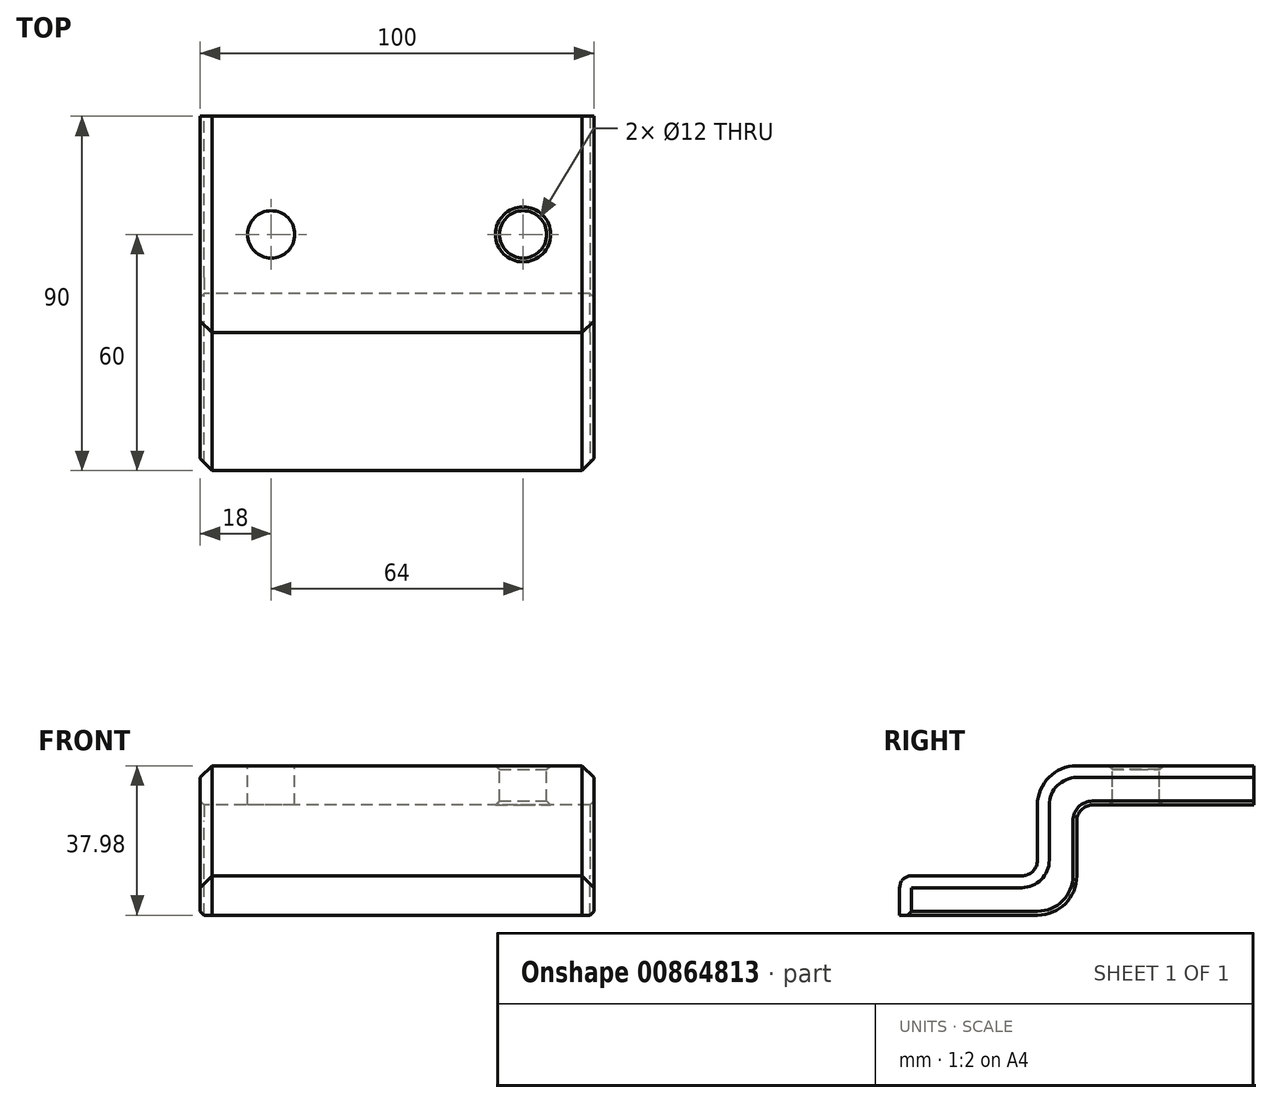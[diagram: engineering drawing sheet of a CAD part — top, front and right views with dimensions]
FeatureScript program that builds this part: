
annotation { "Feature Type Name" : "Feature", "Feature Type Description" : "" }
export const myFeature = defineFeature(function(context is Context, id is Id, definition is map)
    precondition{}
    {
        {
            var Q0;
            Q0=qCreatedBy(makeId("Right.planeOp"),FACE);
            var sketch = newSketch(context, id + "F0", { "sketchPlane" : qUnion([Q0])});
            skLineSegment(sketch, "E0", {"start": v(0, 75.8) * mm, "end": v(0, -75.8) * mm, "construction": true});
            skLineSegment(sketch, "E1", {"start": v(0, 36.2) * mm, "end": v(-45, 36.2) * mm});
            skLineSegment(sketch, "E2", {"start": v(-55, 26.2) * mm, "end": v(-55, 12.2) * mm});
            skLineSegment(sketch, "E3", {"start": v(-59, 8.2) * mm, "end": v(-87, 8.2) * mm});
            skLineSegment(sketch, "E4", {"start": v(-90, 5.2) * mm, "end": v(-90, -1.8) * mm});
            skLineSegment(sketch, "E5", {"start": v(0, 26.2) * mm, "end": v(0, 36.2) * mm});
            skPoint(sketch, "E6.visualSharp", {"position": v(-55, 36.2) * mm});
            skArc(sketch, "E6.filletArc", {"start": v(-45, 36.2) * mm, "mid": v(-52.07, 33.26) * mm, "end": v(-55, 26.2) * mm});
            skArc(sketch, "E7.filletArc", {"start": v(-59, 8.2) * mm, "mid": v(-56.17, 9.38) * mm, "end": v(-55, 12.2) * mm});
            skPoint(sketch, "E8.visualSharp", {"position": v(-90, 8.2) * mm});
            skArc(sketch, "E8.filletArc", {"start": v(-87, 8.2) * mm, "mid": v(-89.12, 7.33) * mm, "end": v(-90, 5.2) * mm});
            skLineSegment(sketch, "E9", {"start": v(0, 26.2) * mm, "end": v(-41, 26.2) * mm});
            skLineSegment(sketch, "E10", {"start": v(-90, -1.8) * mm, "end": v(-55, -1.8) * mm});
            skLineSegment(sketch, "E11", {"start": v(-45, 8.2) * mm, "end": v(-45, 22.2) * mm});
            skPoint(sketch, "E12.visualSharp", {"position": v(-45, -1.8) * mm});
            skArc(sketch, "E12.filletArc", {"start": v(-55, -1.8) * mm, "mid": v(-47.93, 1.14) * mm, "end": v(-45, 8.2) * mm});
            skArc(sketch, "E13.filletArc", {"start": v(-41, 26.2) * mm, "mid": v(-43.83, 25.02) * mm, "end": v(-45, 22.2) * mm});
            skArc(sketch, "E14.MirrorCS", {"start": v(59, 8.2) * mm, "mid": v(56.17, 9.38) * mm, "end": v(55, 12.2) * mm});
            skArc(sketch, "E15.MirrorCS", {"start": v(87, 8.2) * mm, "mid": v(89.12, 7.33) * mm, "end": v(90, 5.2) * mm});
            skArc(sketch, "E16.MirrorCS", {"start": v(41, 26.2) * mm, "mid": v(43.83, 25.02) * mm, "end": v(45, 22.2) * mm});
            skLineSegment(sketch, "E17.MirrorCS", {"start": v(90, -1.8) * mm, "end": v(55, -1.8) * mm});
            skLineSegment(sketch, "E18.MirrorCS", {"start": v(55, 26.2) * mm, "end": v(55, 12.2) * mm});
            skPoint(sketch, "E19.MirrorP", {"position": v(45, -1.8) * mm});
            skPoint(sketch, "E20.MirrorP", {"position": v(90, 8.2) * mm});
            skLineSegment(sketch, "E21.MirrorCS", {"start": v(90, 5.2) * mm, "end": v(90, -1.8) * mm});
            skPoint(sketch, "E22.MirrorP", {"position": v(55, 36.2) * mm});
            skPoint(sketch, "E23.MirrorP", {"position": v(45, 26.2) * mm});
            skLineSegment(sketch, "E24.MirrorCS", {"start": v(45, 8.2) * mm, "end": v(45, 22.2) * mm});
            skLineSegment(sketch, "E25.MirrorCS", {"start": v(0, 26.2) * mm, "end": v(41, 26.2) * mm});
            skArc(sketch, "E26.MirrorCS", {"start": v(45, 36.2) * mm, "mid": v(52.07, 33.26) * mm, "end": v(55, 26.2) * mm});
            skLineSegment(sketch, "E27.MirrorCS", {"start": v(59, 8.2) * mm, "end": v(87, 8.2) * mm});
            skArc(sketch, "E28.MirrorCS", {"start": v(55, -1.8) * mm, "mid": v(47.93, 1.14) * mm, "end": v(45, 8.2) * mm});
            skLineSegment(sketch, "E29.MirrorCS", {"start": v(0, 36.2) * mm, "end": v(45, 36.2) * mm});
            skSolve(sketch);
        }
        {
            var Q0;
            Q0=makeQuery(id+"F0.imprint","IMPRINT",FACE,{"disambiguationData":[TD([[makeQuery(id+"F0.imprint","IMPRINT",EDGE,{"derivedFrom":sQuery(id+"F0.wireOp",EDGE,"E14.MirrorCS")}),1.0]])]});
            var Q1;
            Q1=makeQuery(id+"F0.imprint","IMPRINT",FACE,{"disambiguationData":[TD([[makeQuery(id+"F0.imprint","IMPRINT",EDGE,{"derivedFrom":sQuery(id+"F0.wireOp",EDGE,"E1")}),1.0]])]});
            extrude(context, id + "F1", {"entities" : qUnion([Q0, Q1]), "depth" : 100 * mm, "offsetDistance" : 25 * mm});
        }
        {
            var Q0;
            Q0=makeQuery(id+"F1.opExtrude","CAP_EDGE",EDGE,{"disambiguationData":[OSD([sQuery(id+"F0.wireOp",EDGE,"E4")])],"isStart":true});
            var Q1;
            Q1=makeQuery(id+"F1.opExtrude","CAP_EDGE",EDGE,{"disambiguationData":[OSD([sQuery(id+"F0.wireOp",EDGE,"E8.filletArc")])],"isStart":true});
            var Q2;
            Q2=makeQuery(id+"F1.opExtrude","CAP_EDGE",EDGE,{"disambiguationData":[OSD([sQuery(id+"F0.wireOp",EDGE,"E3")])],"isStart":true});
            var Q3;
            Q3=makeQuery(id+"F1.opExtrude","CAP_EDGE",EDGE,{"disambiguationData":[OSD([sQuery(id+"F0.wireOp",EDGE,"E7.filletArc")])],"isStart":true});
            var Q4;
            Q4=makeQuery(id+"F1.opExtrude","CAP_EDGE",EDGE,{"disambiguationData":[OSD([sQuery(id+"F0.wireOp",EDGE,"E2")])],"isStart":true});
            var Q5;
            Q5=makeQuery(id+"F1.opExtrude","CAP_EDGE",EDGE,{"disambiguationData":[OSD([sQuery(id+"F0.wireOp",EDGE,"E6.filletArc")])],"isStart":true});
            var Q6;
            Q6=makeQuery(id+"F1.opExtrude","CAP_EDGE",EDGE,{"disambiguationData":[OSD([sQuery(id+"F0.wireOp",EDGE,"E1"),sQuery(id+"F0.wireOp",EDGE,"E29.MirrorCS")])],"isStart":true});
            var Q7;
            Q7=makeQuery(id+"F1.opExtrude","CAP_EDGE",EDGE,{"disambiguationData":[OSD([sQuery(id+"F0.wireOp",EDGE,"E26.MirrorCS")])],"isStart":true});
            var Q8;
            Q8=makeQuery(id+"F1.opExtrude","CAP_EDGE",EDGE,{"disambiguationData":[OSD([sQuery(id+"F0.wireOp",EDGE,"E1"),sQuery(id+"F0.wireOp",EDGE,"E29.MirrorCS")])],"isStart":false});
            chamfer(context, id + "F2", {"entities" : qUnion([Q0, Q1, Q2, Q3, Q4, Q5, Q6, Q7, Q8]), "width" : 3 * mm, "tangentPropagation" : true});
        }
        {
            var Q0;
            Q0=makeQuery(id+"F1.opExtrude","CAP_EDGE",EDGE,{"disambiguationData":[OSD([sQuery(id+"F0.wireOp",EDGE,"E9"),sQuery(id+"F0.wireOp",EDGE,"E25.MirrorCS")])],"isStart":false});
            var Q1;
            Q1=makeQuery(id+"F1.opExtrude","CAP_EDGE",EDGE,{"disambiguationData":[OSD([sQuery(id+"F0.wireOp",EDGE,"E9"),sQuery(id+"F0.wireOp",EDGE,"E25.MirrorCS")])],"isStart":true});
            chamfer(context, id + "F3", {"entities" : qUnion([Q0, Q1]), "width" : 1 * mm, "tangentPropagation" : true});
        }
        {
            var Q0;
            Q0=makeQuery(id+"F1.opExtrude","SWEPT_FACE",FACE,{"disambiguationData":[OSD([sQuery(id+"F0.wireOp",EDGE,"E1"),sQuery(id+"F0.wireOp",EDGE,"E29.MirrorCS")])]});
            var sketch = newSketch(context, id + "F4", { "sketchPlane" : qUnion([Q0])});
            skLineSegment(sketch, "E30", {"start": v(3, 30) * mm, "end": v(97, 30) * mm, "construction": true});
            skLineSegment(sketch, "E31", {"start": v(3, -30) * mm, "end": v(97, -30) * mm, "construction": true});
            skLineSegment(sketch, "E32", {"start": v(18, 45) * mm, "end": v(18, -45) * mm, "construction": true});
            skLineSegment(sketch, "E33", {"start": v(82, 45) * mm, "end": v(82, -45) * mm, "construction": true});
            skCircle(sketch, "E34", {"center": v(18, 30) * mm, "radius": 6 * mm});
            skCircle(sketch, "E35", {"center": v(82, 30) * mm, "radius": 6 * mm});
            skCircle(sketch, "E36", {"center": v(82, -30) * mm, "radius": 6 * mm});
            skCircle(sketch, "E37", {"center": v(18, -30) * mm, "radius": 6 * mm});
            skSolve(sketch);
        }
        {
            var Q0;
            Q0=makeQuery(id+"F4.imprint","IMPRINT",FACE,{"disambiguationData":[TD([[makeQuery(id+"F4.imprint","IMPRINT",EDGE,{"derivedFrom":sQuery(id+"F4.wireOp",EDGE,"E37")}),1.0]])]});
            var Q1;
            Q1=makeQuery(id+"F4.imprint","IMPRINT",FACE,{"disambiguationData":[TD([[makeQuery(id+"F4.imprint","IMPRINT",EDGE,{"derivedFrom":sQuery(id+"F4.wireOp",EDGE,"E36")}),1.0]])]});
            var Q2;
            Q2=makeQuery(id+"F4.imprint","IMPRINT",FACE,{"disambiguationData":[TD([[makeQuery(id+"F4.imprint","IMPRINT",EDGE,{"derivedFrom":sQuery(id+"F4.wireOp",EDGE,"E35")}),1.0]])]});
            var Q3;
            Q3=makeQuery(id+"F4.imprint","IMPRINT",FACE,{"disambiguationData":[TD([[makeQuery(id+"F4.imprint","IMPRINT",EDGE,{"derivedFrom":sQuery(id+"F4.wireOp",EDGE,"E34")}),1.0]])]});
            extrude(context, id + "F5", {"entities" : qUnion([Q0, Q1, Q2, Q3]), "operationType" : NewBodyOperationType.REMOVE, "oppositeDirection" : true, "depth" : 10 * mm, "offsetDistance" : 25 * mm});
        }
        {
            var Q0;
            Q0=makeQuery(id+"F5.boolean.opBoolean","COPY",EDGE,{"derivedFrom":makeQuery(id+"F5.opExtrude","CAP_EDGE",EDGE,{"disambiguationData":[OSD([sQuery(id+"F4.wireOp",EDGE,"E34")])],"isStart":true})});
            var Q1;
            Q1=makeQuery(id+"F5.boolean.opBoolean","COPY",EDGE,{"derivedFrom":makeQuery(id+"F5.opExtrude","CAP_EDGE",EDGE,{"disambiguationData":[OSD([sQuery(id+"F4.wireOp",EDGE,"E35")])],"isStart":true})});
            var Q2;
            Q2=makeQuery(id+"F5.boolean.opBoolean","COPY",FACE,{"derivedFrom":makeQuery(id+"F5.opExtrude","SWEPT_FACE",FACE,{"disambiguationData":[OSD([sQuery(id+"F4.wireOp",EDGE,"E36")])]})});
            var Q3;
            Q3=makeQuery(id+"F5.boolean.opBoolean","COPY",EDGE,{"derivedFrom":makeQuery(id+"F5.opExtrude","CAP_EDGE",EDGE,{"disambiguationData":[OSD([sQuery(id+"F4.wireOp",EDGE,"E37")])],"isStart":true})});
            var Q4;
            Q4=makeQuery(id+"F5.boolean.opBoolean","COPY",EDGE,{"derivedFrom":makeQuery(id+"F5.opExtrude","CAP_EDGE",EDGE,{"disambiguationData":[OSD([sQuery(id+"F4.wireOp",EDGE,"E35")])],"isStart":false})});
            var Q5;
            Q5=makeQuery(id+"F5.boolean.opBoolean","COPY",EDGE,{"derivedFrom":makeQuery(id+"F5.opExtrude","CAP_EDGE",EDGE,{"disambiguationData":[OSD([sQuery(id+"F4.wireOp",EDGE,"E34")])],"isStart":false})});
            var Q6;
            Q6=makeQuery(id+"F5.boolean.opBoolean","COPY",EDGE,{"derivedFrom":makeQuery(id+"F5.opExtrude","CAP_EDGE",EDGE,{"disambiguationData":[OSD([sQuery(id+"F4.wireOp",EDGE,"E37")])],"isStart":false})});
            chamfer(context, id + "F6", {"entities" : qUnion([Q0, Q1, Q2, Q3, Q4, Q5, Q6]), "width" : 1 * mm, "tangentPropagation" : true});
        }
    });
